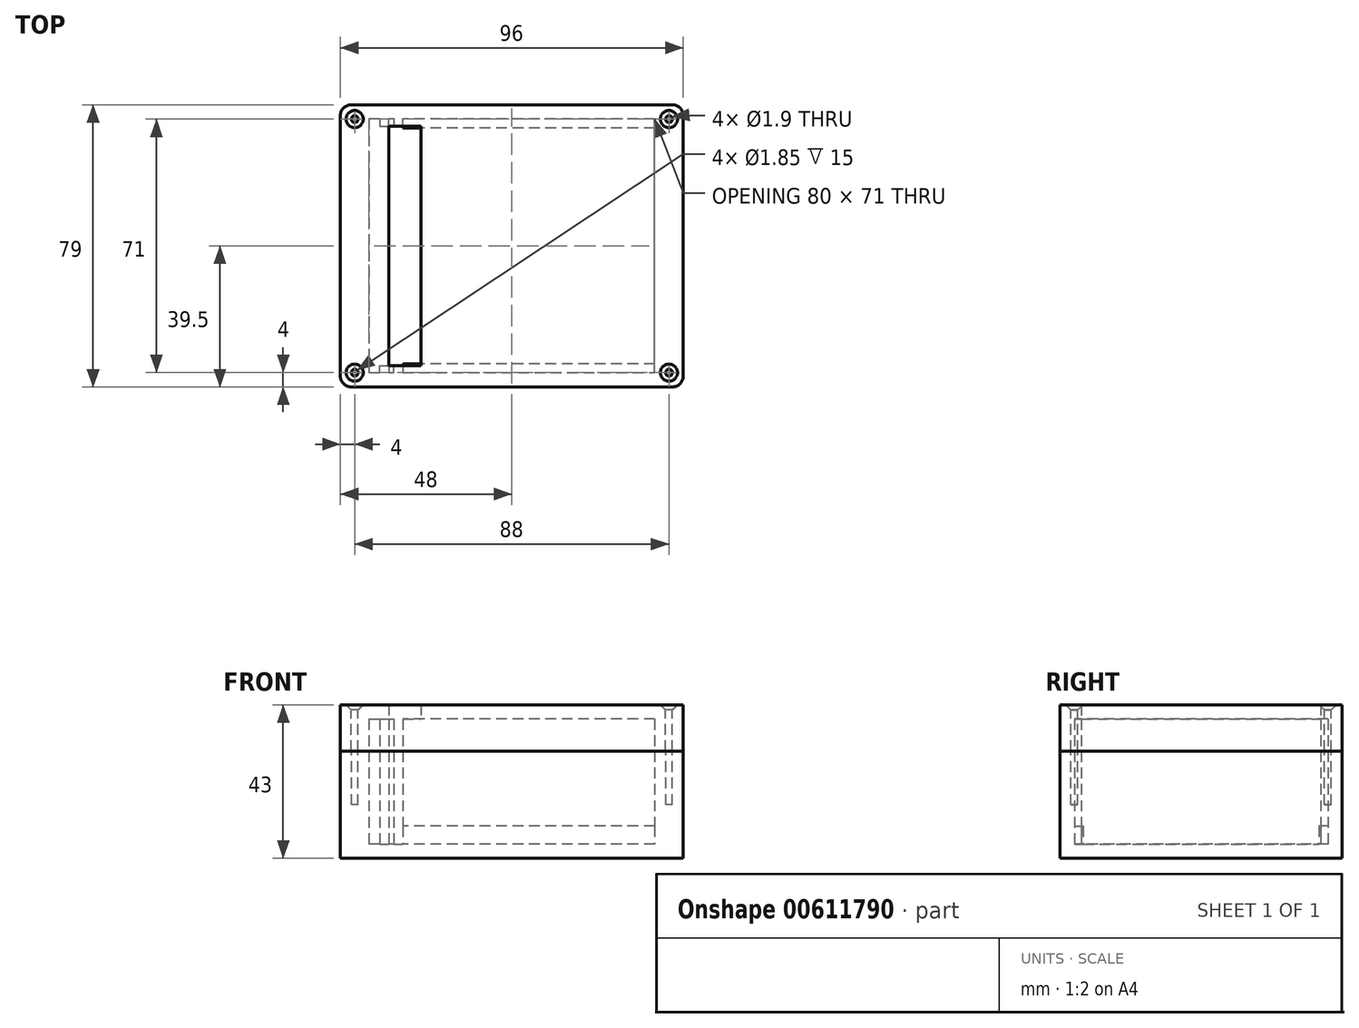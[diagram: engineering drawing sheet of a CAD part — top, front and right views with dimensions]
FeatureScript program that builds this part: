
annotation { "Feature Type Name" : "Feature", "Feature Type Description" : "" }
export const myFeature = defineFeature(function(context is Context, id is Id, definition is map)
    precondition{}
    {
        {
            var Q0;
            Q0=qCreatedBy(makeId("Top.planeOp"),FACE);
            var sketch = newSketch(context, id + "F0", { "sketchPlane" : qUnion([Q0])});
            skLineSegment(sketch, "E0", {"start": v(-88, -4) * mm, "end": v(-88, -75) * mm});
            skLineSegment(sketch, "E1", {"start": v(-8, -75) * mm, "end": v(-8, -4) * mm});
            skLineSegment(sketch, "E2", {"start": v(-8, -4) * mm, "end": v(-78.5, -4) * mm});
            skLineSegment(sketch, "E3", {"start": v(-96, 0) * mm, "end": v(-96, -79) * mm});
            skLineSegment(sketch, "E4", {"start": v(-96, -79) * mm, "end": v(0, -79) * mm});
            skLineSegment(sketch, "E5", {"start": v(0, -79) * mm, "end": v(0, 0) * mm});
            skLineSegment(sketch, "E6", {"start": v(0, 0) * mm, "end": v(-96, 0) * mm});
            skLineSegment(sketch, "E7", {"start": v(-85, -4) * mm, "end": v(-85, -6) * mm});
            skLineSegment(sketch, "E8", {"start": v(-85, -6) * mm, "end": v(-82.5, -6) * mm});
            skLineSegment(sketch, "E9", {"start": v(-82.5, -6) * mm, "end": v(-82.5, -4) * mm});
            skLineSegment(sketch, "E10", {"start": v(-81, -4) * mm, "end": v(-81, -6) * mm});
            skLineSegment(sketch, "E11", {"start": v(-81, -6) * mm, "end": v(-78.5, -6) * mm});
            skLineSegment(sketch, "E12", {"start": v(-78.5, -6) * mm, "end": v(-78.5, -4) * mm});
            skLineSegment(sketch, "E13", {"start": v(-96, -39.5) * mm, "end": v(0, -39.5) * mm, "construction": true});
            skLineSegment(sketch, "E14.trimOffspring", {"start": v(-81, -4) * mm, "end": v(-82.5, -4) * mm});
            skLineSegment(sketch, "E15.trimOffspring", {"start": v(-85, -4) * mm, "end": v(-88, -4) * mm});
            skLineSegment(sketch, "E16.MirrorCS", {"start": v(-85, -75) * mm, "end": v(-85, -73) * mm});
            skLineSegment(sketch, "E17.MirrorCS", {"start": v(-85, -73) * mm, "end": v(-82.5, -73) * mm});
            skLineSegment(sketch, "E18.MirrorCS", {"start": v(-78.5, -73) * mm, "end": v(-78.5, -75) * mm});
            skLineSegment(sketch, "E19.MirrorCS", {"start": v(-82.5, -73) * mm, "end": v(-82.5, -75) * mm});
            skLineSegment(sketch, "E20.MirrorCS", {"start": v(-81, -75) * mm, "end": v(-81, -73) * mm});
            skLineSegment(sketch, "E21.MirrorCS", {"start": v(-81, -73) * mm, "end": v(-78.5, -73) * mm});
            skLineSegment(sketch, "E22.trimOffspring", {"start": v(-78.5, -75) * mm, "end": v(-8, -75) * mm});
            skLineSegment(sketch, "E23", {"start": v(-88, -75) * mm, "end": v(-85, -75) * mm});
            skLineSegment(sketch, "E24", {"start": v(-82.5, -75) * mm, "end": v(-81, -75) * mm});
            skSolve(sketch);
        }
        {
            var Q0;
            Q0 = qSketchRegion(id + "F0", true);
            extrude(context, id + "F1", {"entities" : qUnion([Q0]), "depth" : 26 * mm, "offsetDistance" : 25 * mm});
        }
        {
            var Q0;
            Q0=qCreatedBy(makeId("Top.planeOp"),FACE);
            var sketch = newSketch(context, id + "F2", { "sketchPlane" : qUnion([Q0])});
            skLineSegment(sketch, "E25.bottom", {"start": v(0, 0) * mm, "end": v(-96, 0) * mm});
            skLineSegment(sketch, "E25.top", {"start": v(0, -79) * mm, "end": v(-96, -79) * mm});
            skLineSegment(sketch, "E25.left", {"start": v(0, 0) * mm, "end": v(0, -79) * mm});
            skLineSegment(sketch, "E25.right", {"start": v(-96, 0) * mm, "end": v(-96, -79) * mm});
            skSolve(sketch);
        }
        {
            var Q0;
            Q0 = qSketchRegion(id + "F2", true);
            extrude(context, id + "F3", {"entities" : qUnion([Q0]), "operationType" : NewBodyOperationType.ADD, "oppositeDirection" : true, "depth" : 4 * mm, "offsetDistance" : 25 * mm});
        }
        {
            var Q0;
            Q0=qCreatedBy(makeId("Top.planeOp"),FACE);
            var sketch = newSketch(context, id + "F4", { "sketchPlane" : qUnion([Q0])});
            skLineSegment(sketch, "E26.bottom", {"start": v(-8, -4) * mm, "end": v(-78.5, -4) * mm});
            skLineSegment(sketch, "E26.top", {"start": v(-8, -6.5) * mm, "end": v(-78.5, -6.5) * mm});
            skLineSegment(sketch, "E26.left", {"start": v(-8, -4) * mm, "end": v(-8, -6.5) * mm});
            skLineSegment(sketch, "E26.right", {"start": v(-78.5, -4) * mm, "end": v(-78.5, -6.5) * mm});
            skLineSegment(sketch, "E27", {"start": v(-88, -39.5) * mm, "end": v(-8, -39.5) * mm, "construction": true});
            skLineSegment(sketch, "E28.MirrorCS", {"start": v(-8, -72.5) * mm, "end": v(-78.5, -72.5) * mm});
            skLineSegment(sketch, "E29.MirrorCS", {"start": v(-78.5, -75) * mm, "end": v(-78.5, -72.5) * mm});
            skLineSegment(sketch, "E30.MirrorCS", {"start": v(-8, -75) * mm, "end": v(-8, -72.5) * mm});
            skLineSegment(sketch, "E31.MirrorCS", {"start": v(-8, -75) * mm, "end": v(-78.5, -75) * mm});
            skSolve(sketch);
        }
        {
            var Q0;
            Q0 = qSketchRegion(id + "F4", true);
            extrude(context, id + "F5", {"entities" : qUnion([Q0]), "operationType" : NewBodyOperationType.ADD, "depth" : 5 * mm, "offsetDistance" : 25 * mm});
        }
        {
            var Q0;
            Q0=makeQuery(id+"F1.opExtrude","CAP_FACE",FACE,{"disambiguationData":[OSD([sQuery(id+"F0.wireOp",EDGE,"E0"),sQuery(id+"F0.wireOp",EDGE,"E1"),sQuery(id+"F0.wireOp",EDGE,"E2"),sQuery(id+"F0.wireOp",EDGE,"E3"),sQuery(id+"F0.wireOp",EDGE,"E4"),sQuery(id+"F0.wireOp",EDGE,"E5"),sQuery(id+"F0.wireOp",EDGE,"E6"),sQuery(id+"F0.wireOp",EDGE,"E7"),sQuery(id+"F0.wireOp",EDGE,"E8"),sQuery(id+"F0.wireOp",EDGE,"E9"),sQuery(id+"F0.wireOp",EDGE,"E10"),sQuery(id+"F0.wireOp",EDGE,"E11"),sQuery(id+"F0.wireOp",EDGE,"E12"),sQuery(id+"F0.wireOp",EDGE,"E14.trimOffspring"),sQuery(id+"F0.wireOp",EDGE,"E15.trimOffspring"),sQuery(id+"F0.wireOp",EDGE,"E16.MirrorCS"),sQuery(id+"F0.wireOp",EDGE,"E17.MirrorCS"),sQuery(id+"F0.wireOp",EDGE,"E18.MirrorCS"),sQuery(id+"F0.wireOp",EDGE,"E19.MirrorCS"),sQuery(id+"F0.wireOp",EDGE,"E20.MirrorCS"),sQuery(id+"F0.wireOp",EDGE,"E21.MirrorCS"),sQuery(id+"F0.wireOp",EDGE,"E22.trimOffspring"),sQuery(id+"F0.wireOp",EDGE,"E23"),sQuery(id+"F0.wireOp",EDGE,"E24")])],"isStart":false});
            var sketch = newSketch(context, id + "F6", { "sketchPlane" : qUnion([Q0])});
            skLineSegment(sketch, "E32.0.0", {"start": v(0, -79) * mm, "end": v(0, 0) * mm});
            skLineSegment(sketch, "E32.0.1", {"start": v(0, 0) * mm, "end": v(-96, 0) * mm});
            skLineSegment(sketch, "E32.0.2", {"start": v(-96, 0) * mm, "end": v(-96, -79) * mm});
            skLineSegment(sketch, "E32.0.3", {"start": v(-96, -79) * mm, "end": v(0, -79) * mm});
            skLineSegment(sketch, "E33", {"start": v(-88, -4) * mm, "end": v(-85, -4) * mm});
            skLineSegment(sketch, "E34", {"start": v(-85, -4) * mm, "end": v(-85, -6) * mm});
            skLineSegment(sketch, "E35", {"start": v(-85, -6) * mm, "end": v(-82.5, -6) * mm});
            skLineSegment(sketch, "E36", {"start": v(-82.5, -6) * mm, "end": v(-82.5, -4) * mm});
            skLineSegment(sketch, "E37", {"start": v(-82.5, -4) * mm, "end": v(-81, -4) * mm});
            skLineSegment(sketch, "E38", {"start": v(-81, -4) * mm, "end": v(-81, -6) * mm});
            skLineSegment(sketch, "E39", {"start": v(-81, -6) * mm, "end": v(-78.5, -6) * mm});
            skLineSegment(sketch, "E40", {"start": v(-78.5, -6) * mm, "end": v(-78.5, -4) * mm});
            skLineSegment(sketch, "E41", {"start": v(-78.5, -4) * mm, "end": v(-8, -4) * mm});
            skLineSegment(sketch, "E42", {"start": v(-8, -4) * mm, "end": v(-8, -75) * mm});
            skLineSegment(sketch, "E43", {"start": v(-8, -75) * mm, "end": v(-78.5, -75) * mm});
            skLineSegment(sketch, "E44", {"start": v(-78.5, -75) * mm, "end": v(-78.5, -73) * mm});
            skLineSegment(sketch, "E45", {"start": v(-78.5, -73) * mm, "end": v(-81, -73) * mm});
            skLineSegment(sketch, "E46", {"start": v(-81, -73) * mm, "end": v(-81, -75) * mm});
            skLineSegment(sketch, "E47", {"start": v(-81, -75) * mm, "end": v(-82.5, -75) * mm});
            skLineSegment(sketch, "E48", {"start": v(-82.5, -75) * mm, "end": v(-82.5, -73) * mm});
            skLineSegment(sketch, "E49", {"start": v(-82.5, -73) * mm, "end": v(-85, -73) * mm});
            skLineSegment(sketch, "E50", {"start": v(-85, -73) * mm, "end": v(-85, -75) * mm});
            skLineSegment(sketch, "E51", {"start": v(-85, -75) * mm, "end": v(-88, -75) * mm});
            skLineSegment(sketch, "E52", {"start": v(-88, -75) * mm, "end": v(-88, -4) * mm});
            skSolve(sketch);
        }
        {
            var Q0;
            Q0=makeQuery(id+"F6.imprint","IMPRINT",FACE,{"disambiguationData":[TD([[makeQuery(id+"F6.imprint","IMPRINT",EDGE,{"derivedFrom":sQuery(id+"F6.wireOp",EDGE,"E32.0.0")}),1.0]])]});
            extrude(context, id + "F7", {"entities" : qUnion([Q0]), "depth" : 9 * mm, "offsetDistance" : 25 * mm});
        }
        {
            var Q0;
            Q0=makeQuery(id+"F7.opExtrude","CAP_FACE",FACE,{"disambiguationData":[OSD([sQuery(id+"F6.wireOp",EDGE,"E32.0.0"),sQuery(id+"F6.wireOp",EDGE,"E32.0.1"),sQuery(id+"F6.wireOp",EDGE,"E32.0.2"),sQuery(id+"F6.wireOp",EDGE,"E32.0.3"),sQuery(id+"F6.wireOp",EDGE,"E33"),sQuery(id+"F6.wireOp",EDGE,"E34"),sQuery(id+"F6.wireOp",EDGE,"E35"),sQuery(id+"F6.wireOp",EDGE,"E36"),sQuery(id+"F6.wireOp",EDGE,"E37"),sQuery(id+"F6.wireOp",EDGE,"E38"),sQuery(id+"F6.wireOp",EDGE,"E39"),sQuery(id+"F6.wireOp",EDGE,"E40"),sQuery(id+"F6.wireOp",EDGE,"E41"),sQuery(id+"F6.wireOp",EDGE,"E42"),sQuery(id+"F6.wireOp",EDGE,"E43"),sQuery(id+"F6.wireOp",EDGE,"E44"),sQuery(id+"F6.wireOp",EDGE,"E45"),sQuery(id+"F6.wireOp",EDGE,"E46"),sQuery(id+"F6.wireOp",EDGE,"E47"),sQuery(id+"F6.wireOp",EDGE,"E48"),sQuery(id+"F6.wireOp",EDGE,"E49"),sQuery(id+"F6.wireOp",EDGE,"E50"),sQuery(id+"F6.wireOp",EDGE,"E51"),sQuery(id+"F6.wireOp",EDGE,"E52")])],"isStart":false});
            var sketch = newSketch(context, id + "F8", { "sketchPlane" : qUnion([Q0])});
            skLineSegment(sketch, "E53.0.0", {"start": v(-96, -79) * mm, "end": v(0, -79) * mm});
            skLineSegment(sketch, "E53.0.1", {"start": v(0, -79) * mm, "end": v(0, 0) * mm});
            skLineSegment(sketch, "E53.0.2", {"start": v(0, 0) * mm, "end": v(-96, 0) * mm});
            skLineSegment(sketch, "E53.0.3", {"start": v(-96, 0) * mm, "end": v(-96, -79) * mm});
            skSolve(sketch);
        }
        {
            var Q0;
            Q0 = qSketchRegion(id + "F8", true);
            extrude(context, id + "F9", {"entities" : qUnion([Q0]), "operationType" : NewBodyOperationType.ADD, "depth" : 4 * mm, "offsetDistance" : 25 * mm});
        }
        {
            var Q0;
            Q0=makeQuery(id+"F9.opExtrude","CAP_FACE",FACE,{"disambiguationData":[OSD([sQuery(id+"F8.wireOp",EDGE,"E53.0.0"),sQuery(id+"F8.wireOp",EDGE,"E53.0.1"),sQuery(id+"F8.wireOp",EDGE,"E53.0.2"),sQuery(id+"F8.wireOp",EDGE,"E53.0.3")])],"isStart":true});
            var sketch = newSketch(context, id + "F10", { "sketchPlane" : qUnion([Q0])});
            skLineSegment(sketch, "E54.bottom", {"start": v(-82.5, 73) * mm, "end": v(-73.5, 73) * mm});
            skLineSegment(sketch, "E54.top", {"start": v(-82.5, 6) * mm, "end": v(-73.5, 6) * mm});
            skLineSegment(sketch, "E54.left", {"start": v(-82.5, 73) * mm, "end": v(-82.5, 6) * mm});
            skLineSegment(sketch, "E54.right", {"start": v(-73.5, 73) * mm, "end": v(-73.5, 6) * mm});
            skSolve(sketch);
        }
        {
            var Q0;
            Q0 = qSketchRegion(id + "F10", true);
            extrude(context, id + "F11", {"entities" : qUnion([Q0]), "operationType" : NewBodyOperationType.REMOVE, "oppositeDirection" : true, "depth" : 10 * mm, "offsetDistance" : 25 * mm});
        }
        {
            var Q0;
            Q0=makeQuery(id+"F1.opExtrude","CAP_FACE",FACE,{"disambiguationData":[OSD([sQuery(id+"F0.wireOp",EDGE,"E0"),sQuery(id+"F0.wireOp",EDGE,"E1"),sQuery(id+"F0.wireOp",EDGE,"E2"),sQuery(id+"F0.wireOp",EDGE,"E3"),sQuery(id+"F0.wireOp",EDGE,"E4"),sQuery(id+"F0.wireOp",EDGE,"E5"),sQuery(id+"F0.wireOp",EDGE,"E6"),sQuery(id+"F0.wireOp",EDGE,"E7"),sQuery(id+"F0.wireOp",EDGE,"E8"),sQuery(id+"F0.wireOp",EDGE,"E9"),sQuery(id+"F0.wireOp",EDGE,"E10"),sQuery(id+"F0.wireOp",EDGE,"E11"),sQuery(id+"F0.wireOp",EDGE,"E12"),sQuery(id+"F0.wireOp",EDGE,"E14.trimOffspring"),sQuery(id+"F0.wireOp",EDGE,"E15.trimOffspring"),sQuery(id+"F0.wireOp",EDGE,"E16.MirrorCS"),sQuery(id+"F0.wireOp",EDGE,"E17.MirrorCS"),sQuery(id+"F0.wireOp",EDGE,"E18.MirrorCS"),sQuery(id+"F0.wireOp",EDGE,"E19.MirrorCS"),sQuery(id+"F0.wireOp",EDGE,"E20.MirrorCS"),sQuery(id+"F0.wireOp",EDGE,"E21.MirrorCS"),sQuery(id+"F0.wireOp",EDGE,"E22.trimOffspring"),sQuery(id+"F0.wireOp",EDGE,"E23"),sQuery(id+"F0.wireOp",EDGE,"E24")])],"isStart":false});
            var sketch = newSketch(context, id + "F12", { "sketchPlane" : qUnion([Q0])});
            skLineSegment(sketch, "E55", {"start": v(-8, -8) * mm, "end": v(0, -8) * mm, "construction": true});
            skLineSegment(sketch, "E56", {"start": v(0, -8) * mm, "end": v(0, 0) * mm, "construction": true});
            skLineSegment(sketch, "E57", {"start": v(-4, -8) * mm, "end": v(-4, -4) * mm, "construction": true});
            skLineSegment(sketch, "E58", {"start": v(0, -4) * mm, "end": v(-4, -4) * mm, "construction": true});
            skLineSegment(sketch, "E59", {"start": v(-48, 0) * mm, "end": v(-48, -79) * mm, "construction": true});
            skLineSegment(sketch, "E60", {"start": v(-96, -39.5) * mm, "end": v(0, -39.5) * mm, "construction": true});
            skLineSegment(sketch, "E61.MirrorCS", {"start": v(-8, -71) * mm, "end": v(0, -71) * mm, "construction": true});
            skLineSegment(sketch, "E62.MirrorCS", {"start": v(-4, -71) * mm, "end": v(-4, -75) * mm, "construction": true});
            skLineSegment(sketch, "E63.MirrorCS", {"start": v(0, -75) * mm, "end": v(-4, -75) * mm, "construction": true});
            skLineSegment(sketch, "E64.MirrorCS", {"start": v(-92, -8) * mm, "end": v(-92, -4) * mm, "construction": true});
            skLineSegment(sketch, "E65.MirrorCS", {"start": v(-96, -4) * mm, "end": v(-92, -4) * mm, "construction": true});
            skLineSegment(sketch, "E66.MirrorCS", {"start": v(-88, -8) * mm, "end": v(-96, -8) * mm, "construction": true});
            skLineSegment(sketch, "E67.MirrorCS", {"start": v(-88, -71) * mm, "end": v(-96, -71) * mm, "construction": true});
            skLineSegment(sketch, "E68.MirrorCS", {"start": v(-92, -71) * mm, "end": v(-92, -75) * mm, "construction": true});
            skLineSegment(sketch, "E69.MirrorCS", {"start": v(-96, -75) * mm, "end": v(-92, -75) * mm, "construction": true});
            skCircle(sketch, "E70", {"center": v(-92, -4) * mm, "radius": 0.93 * mm});
            skCircle(sketch, "E71", {"center": v(-4, -4) * mm, "radius": 0.93 * mm});
            skCircle(sketch, "E72", {"center": v(-4, -75) * mm, "radius": 0.93 * mm});
            skCircle(sketch, "E73", {"center": v(-92, -75) * mm, "radius": 0.93 * mm});
            skSolve(sketch);
        }
        {
            var Q0;
            Q0 = qSketchRegion(id + "F12", true);
            extrude(context, id + "F13", {"entities" : qUnion([Q0]), "operationType" : NewBodyOperationType.REMOVE, "depth" : 25 * mm, "offsetDistance" : 25 * mm});
        }
        {
            var Q0;
            Q0=makeQuery(id+"F9.opExtrude","CAP_FACE",FACE,{"disambiguationData":[OSD([sQuery(id+"F8.wireOp",EDGE,"E53.0.0"),sQuery(id+"F8.wireOp",EDGE,"E53.0.1"),sQuery(id+"F8.wireOp",EDGE,"E53.0.2"),sQuery(id+"F8.wireOp",EDGE,"E53.0.3")])],"isStart":false});
            var sketch = newSketch(context, id + "F14", { "sketchPlane" : qUnion([Q0])});
            skPoint(sketch, "E74", {"position": v(-4, -4) * mm});
            skPoint(sketch, "E75", {"position": v(-4, -75) * mm});
            skPoint(sketch, "E76", {"position": v(-92, -75) * mm});
            skPoint(sketch, "E77", {"position": v(-92, -4) * mm});
            skSolve(sketch);
        }
        {
            var Q0;
            Q0=sQuery(id+"F14.wireOp",VERTEX,"E77");
            var Q1;
            Q1=sQuery(id+"F14.wireOp",VERTEX,"E76");
            var Q2;
            Q2=sQuery(id+"F14.wireOp",VERTEX,"E75");
            var Q3;
            Q3=sQuery(id+"F14.wireOp",VERTEX,"E74");
            var Q4;
            Q4=makeQuery(id+"F7.opExtrude","SWEPT_BODY",BODY,{"disambiguationData":[OSD([sQuery(id+"F6.wireOp",EDGE,"E32.0.0"),sQuery(id+"F6.wireOp",EDGE,"E32.0.1"),sQuery(id+"F6.wireOp",EDGE,"E32.0.2"),sQuery(id+"F6.wireOp",EDGE,"E32.0.3"),sQuery(id+"F6.wireOp",EDGE,"E33"),sQuery(id+"F6.wireOp",EDGE,"E34"),sQuery(id+"F6.wireOp",EDGE,"E35"),sQuery(id+"F6.wireOp",EDGE,"E36"),sQuery(id+"F6.wireOp",EDGE,"E37"),sQuery(id+"F6.wireOp",EDGE,"E38"),sQuery(id+"F6.wireOp",EDGE,"E39"),sQuery(id+"F6.wireOp",EDGE,"E40"),sQuery(id+"F6.wireOp",EDGE,"E41"),sQuery(id+"F6.wireOp",EDGE,"E42"),sQuery(id+"F6.wireOp",EDGE,"E43"),sQuery(id+"F6.wireOp",EDGE,"E44"),sQuery(id+"F6.wireOp",EDGE,"E45"),sQuery(id+"F6.wireOp",EDGE,"E46"),sQuery(id+"F6.wireOp",EDGE,"E47"),sQuery(id+"F6.wireOp",EDGE,"E48"),sQuery(id+"F6.wireOp",EDGE,"E49"),sQuery(id+"F6.wireOp",EDGE,"E50"),sQuery(id+"F6.wireOp",EDGE,"E51"),sQuery(id+"F6.wireOp",EDGE,"E52")])]});
            hole(context, id + "F15", {"style" : HoleStyle.C_SINK, "endStyle" : HoleEndStyle.THROUGH, "holeDiameter" : 1.9 * mm, "cSinkDiameter" : 4.8 * mm, "cSinkAngle" : 90 * degree, "majorDiameter" : 5 * mm, "isTappedThrough" : true, "tappedDepth" : 12 * mm, "tapClearance" : 3, "locations" : qUnion([Q0, Q1, Q2, Q3]), "scope" : qUnion([Q4])});
        }
        {
            var Q0;
            Q0 = qSketchRegion(id + "F12", true);
            extrude(context, id + "F16", {"entities" : qUnion([Q0]), "operationType" : NewBodyOperationType.REMOVE, "oppositeDirection" : true, "depth" : 15 * mm, "offsetDistance" : 25 * mm});
        }
        {
            var Q0;
            Q0=makeQuery(id+"F3.boolean.opBoolean","MERGE",EDGE,{"derivedFrom":[makeQuery(id+"F1.opExtrude","SWEPT_EDGE",EDGE,{"disambiguationData":[OSD([sQuery(id+"F0.wireOp",EDGE,"E4"),sQuery(id+"F0.wireOp",EDGE,"E5")])]}),makeQuery(id+"F3.opExtrude","SWEPT_EDGE",EDGE,{"disambiguationData":[OSD([sQuery(id+"F2.wireOp",EDGE,"E25.top"),sQuery(id+"F2.wireOp",EDGE,"E25.left")])]})]});
            var Q1;
            Q1=makeQuery(id+"F9.boolean.opBoolean","MERGE",EDGE,{"derivedFrom":[makeQuery(id+"F7.opExtrude","SWEPT_EDGE",EDGE,{"disambiguationData":[OSD([sQuery(id+"F6.wireOp",EDGE,"E32.0.0"),sQuery(id+"F6.wireOp",EDGE,"E32.0.3")])]}),makeQuery(id+"F9.opExtrude","SWEPT_EDGE",EDGE,{"disambiguationData":[OSD([sQuery(id+"F8.wireOp",EDGE,"E53.0.0"),sQuery(id+"F8.wireOp",EDGE,"E53.0.1")])]})]});
            var Q2;
            Q2=makeQuery(id+"F3.boolean.opBoolean","MERGE",EDGE,{"derivedFrom":[makeQuery(id+"F1.opExtrude","SWEPT_EDGE",EDGE,{"disambiguationData":[OSD([sQuery(id+"F0.wireOp",EDGE,"E3"),sQuery(id+"F0.wireOp",EDGE,"E4")])]}),makeQuery(id+"F3.opExtrude","SWEPT_EDGE",EDGE,{"disambiguationData":[OSD([sQuery(id+"F2.wireOp",EDGE,"E25.top"),sQuery(id+"F2.wireOp",EDGE,"E25.right")])]})]});
            var Q3;
            Q3=makeQuery(id+"F9.boolean.opBoolean","MERGE",EDGE,{"derivedFrom":[makeQuery(id+"F7.opExtrude","SWEPT_EDGE",EDGE,{"disambiguationData":[OSD([sQuery(id+"F6.wireOp",EDGE,"E32.0.2"),sQuery(id+"F6.wireOp",EDGE,"E32.0.3")])]}),makeQuery(id+"F9.opExtrude","SWEPT_EDGE",EDGE,{"disambiguationData":[OSD([sQuery(id+"F8.wireOp",EDGE,"E53.0.0"),sQuery(id+"F8.wireOp",EDGE,"E53.0.3")])]})]});
            var Q4;
            Q4=makeQuery(id+"F9.boolean.opBoolean","MERGE",EDGE,{"derivedFrom":[makeQuery(id+"F7.opExtrude","SWEPT_EDGE",EDGE,{"disambiguationData":[OSD([sQuery(id+"F6.wireOp",EDGE,"E32.0.0"),sQuery(id+"F6.wireOp",EDGE,"E32.0.1")])]}),makeQuery(id+"F9.opExtrude","SWEPT_EDGE",EDGE,{"disambiguationData":[OSD([sQuery(id+"F8.wireOp",EDGE,"E53.0.1"),sQuery(id+"F8.wireOp",EDGE,"E53.0.2")])]})]});
            var Q5;
            Q5=makeQuery(id+"F3.boolean.opBoolean","MERGE",EDGE,{"derivedFrom":[makeQuery(id+"F1.opExtrude","SWEPT_EDGE",EDGE,{"disambiguationData":[OSD([sQuery(id+"F0.wireOp",EDGE,"E5"),sQuery(id+"F0.wireOp",EDGE,"E6")])]}),makeQuery(id+"F3.opExtrude","SWEPT_EDGE",EDGE,{"disambiguationData":[OSD([sQuery(id+"F2.wireOp",EDGE,"E25.bottom"),sQuery(id+"F2.wireOp",EDGE,"E25.left")])]})]});
            var Q6;
            Q6=makeQuery(id+"F3.boolean.opBoolean","MERGE",EDGE,{"derivedFrom":[makeQuery(id+"F1.opExtrude","SWEPT_EDGE",EDGE,{"disambiguationData":[OSD([sQuery(id+"F0.wireOp",EDGE,"E3"),sQuery(id+"F0.wireOp",EDGE,"E6")])]}),makeQuery(id+"F3.opExtrude","SWEPT_EDGE",EDGE,{"disambiguationData":[OSD([sQuery(id+"F2.wireOp",EDGE,"E25.bottom"),sQuery(id+"F2.wireOp",EDGE,"E25.right")])]})]});
            var Q7;
            Q7=makeQuery(id+"F9.boolean.opBoolean","MERGE",EDGE,{"derivedFrom":[makeQuery(id+"F7.opExtrude","SWEPT_EDGE",EDGE,{"disambiguationData":[OSD([sQuery(id+"F6.wireOp",EDGE,"E32.0.1"),sQuery(id+"F6.wireOp",EDGE,"E32.0.2")])]}),makeQuery(id+"F9.opExtrude","SWEPT_EDGE",EDGE,{"disambiguationData":[OSD([sQuery(id+"F8.wireOp",EDGE,"E53.0.2"),sQuery(id+"F8.wireOp",EDGE,"E53.0.3")])]})]});
            fillet(context, id + "F17", {"entities" : qUnion([Q0, Q1, Q2, Q3, Q4, Q5, Q6, Q7]), "radius" : 3 * mm, "tangentPropagation" : true, "allowEdgeOverflow" : false});
        }
    });
